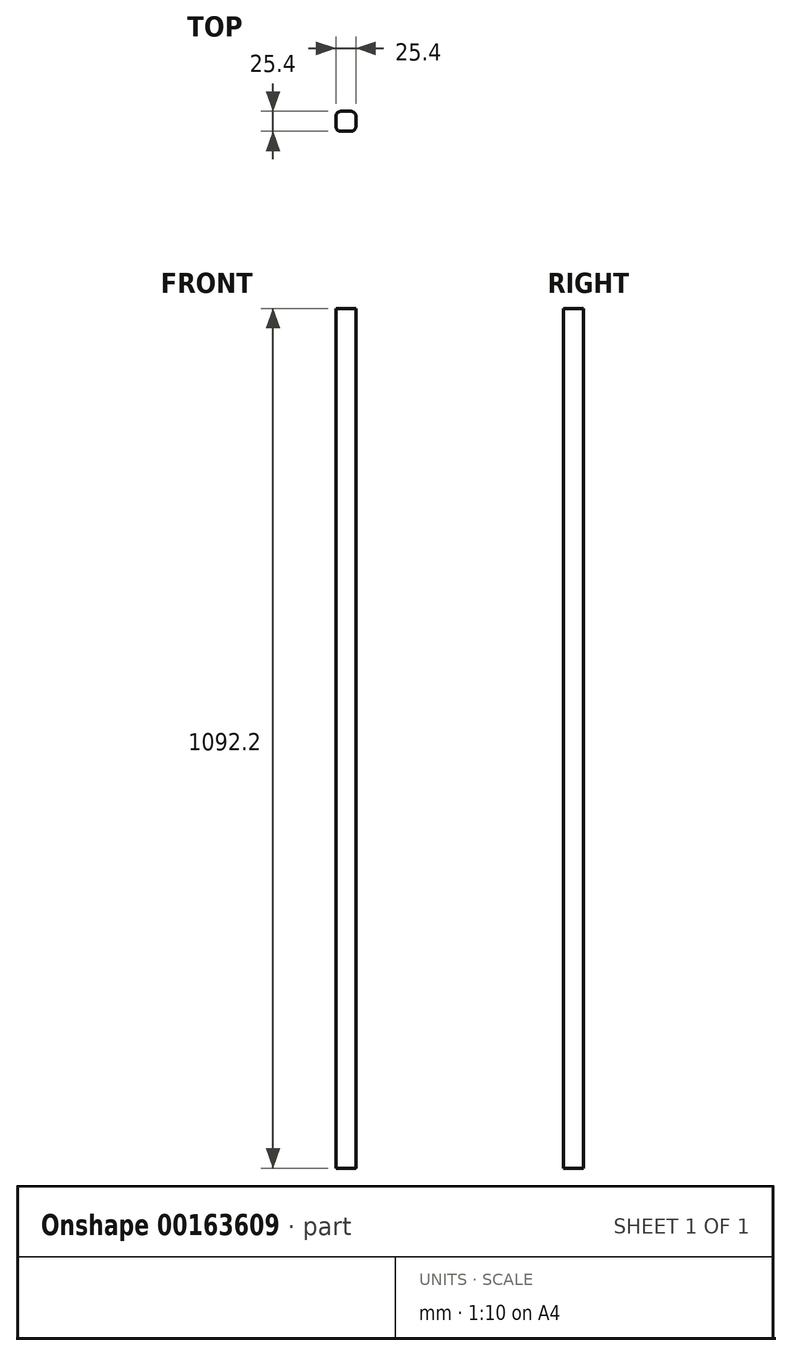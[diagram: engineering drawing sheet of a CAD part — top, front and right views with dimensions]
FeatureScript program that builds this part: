
annotation { "Feature Type Name" : "Feature", "Feature Type Description" : "" }
export const myFeature = defineFeature(function(context is Context, id is Id, definition is map)
    precondition{}
    {
        {
            var Q0;
            Q0=qCreatedBy(makeId("Top.planeOp"),FACE);
            var sketch = newSketch(context, id + "F0", { "sketchPlane" : qUnion([Q0])});
            skLineSegment(sketch, "E0.bottom", {"start": v(6.35, 12.7) * mm, "end": v(-6.35, 12.7) * mm});
            skLineSegment(sketch, "E0.top", {"start": v(6.35, -12.7) * mm, "end": v(-6.35, -12.7) * mm});
            skLineSegment(sketch, "E0.left", {"start": v(12.7, 6.35) * mm, "end": v(12.7, -6.35) * mm});
            skLineSegment(sketch, "E0.right", {"start": v(-12.7, 6.35) * mm, "end": v(-12.7, -6.35) * mm});
            skPoint(sketch, "E0.middle", {"position": v(0, 0) * mm});
            skPoint(sketch, "E1.visualSharp", {"position": v(-12.7, 12.7) * mm});
            skArc(sketch, "E1.filletArc", {"start": v(-6.35, 12.7) * mm, "mid": v(-10.84, 10.84) * mm, "end": v(-12.7, 6.35) * mm});
            skPoint(sketch, "E2.visualSharp", {"position": v(12.7, 12.7) * mm});
            skArc(sketch, "E2.filletArc", {"start": v(12.7, 6.35) * mm, "mid": v(10.84, 10.84) * mm, "end": v(6.35, 12.7) * mm});
            skPoint(sketch, "E3.visualSharp", {"position": v(12.7, -12.7) * mm});
            skArc(sketch, "E3.filletArc", {"start": v(6.35, -12.7) * mm, "mid": v(10.84, -10.84) * mm, "end": v(12.7, -6.35) * mm});
            skPoint(sketch, "E4.visualSharp", {"position": v(-12.7, -12.7) * mm});
            skArc(sketch, "E4.filletArc", {"start": v(-12.7, -6.35) * mm, "mid": v(-10.84, -10.84) * mm, "end": v(-6.35, -12.7) * mm});
            skSolve(sketch);
        }
        {
            var Q0;
            Q0=qSketchRegion(id+"F0",true);
            extrude(context, id + "F1", {"entities" : qUnion([Q0]), "depth" : 1092.2 * mm, "offsetDistance" : 25.4 * mm});
        }
    });
